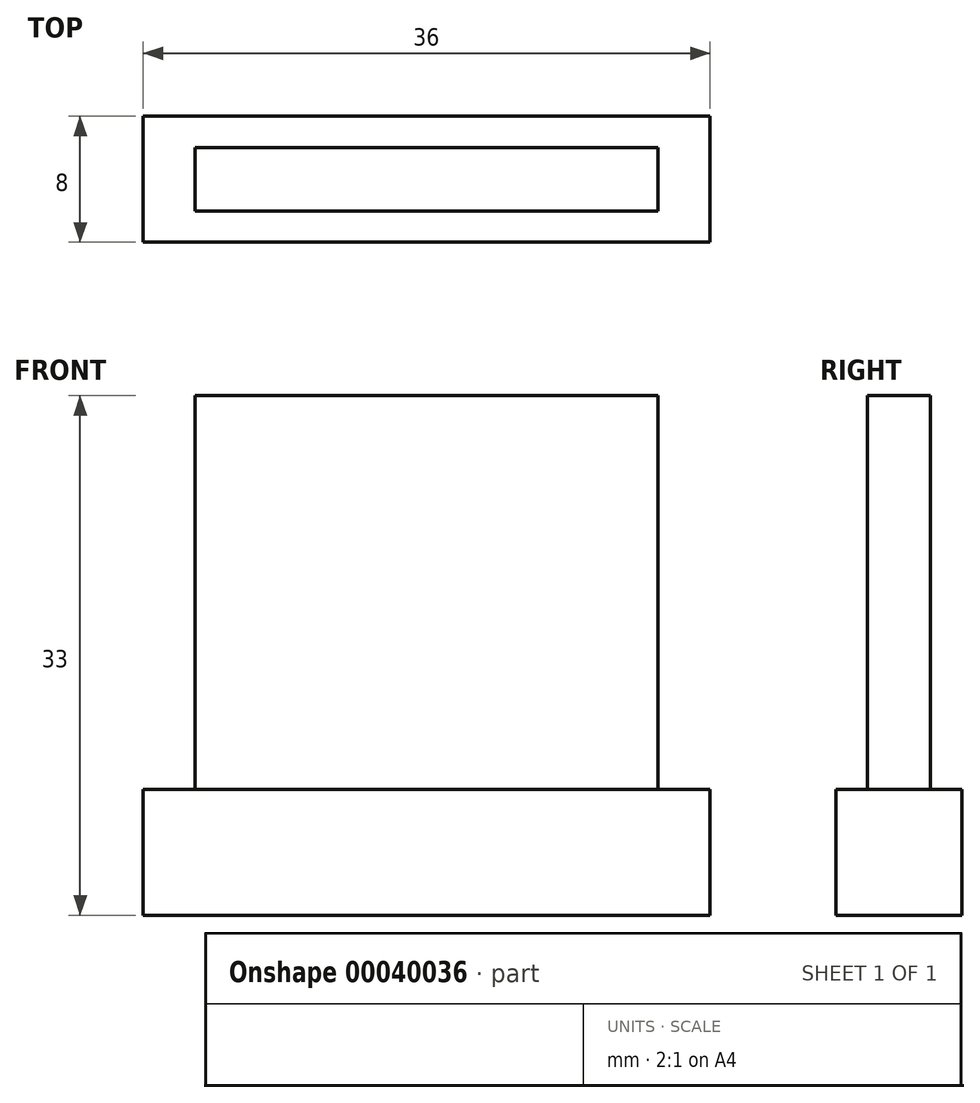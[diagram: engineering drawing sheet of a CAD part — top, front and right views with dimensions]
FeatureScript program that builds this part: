
annotation { "Feature Type Name" : "Feature", "Feature Type Description" : "" }
export const myFeature = defineFeature(function(context is Context, id is Id, definition is map)
    precondition{}
    {
        {
            var Q0;
            Q0=qCreatedBy(makeId("Top.planeOp"),FACE);
            var sketch = newSketch(context, id + "F0", { "sketchPlane" : qUnion([Q0])});
            skLineSegment(sketch, "E0.rect.bottom", {"start": v(18, -4) * mm, "end": v(-18, -4) * mm});
            skLineSegment(sketch, "E0.rect.top", {"start": v(18, 4) * mm, "end": v(-18, 4) * mm});
            skLineSegment(sketch, "E0.rect.left", {"start": v(18, -4) * mm, "end": v(18, 4) * mm});
            skLineSegment(sketch, "E0.rect.right", {"start": v(-18, -4) * mm, "end": v(-18, 4) * mm});
            skPoint(sketch, "E0.rect.middle", {"position": v(0, 0) * mm});
            skSolve(sketch);
        }
        {
            var Q0;
            Q0 = qSketchRegion(id + "F0", true);
            extrude(context, id + "F1", {"entities" : qUnion([Q0]), "depth" : 8 * mm});
        }
        {
            var Q0;
            Q0=makeQuery(id+"F1.opExtrude","CAP_FACE",FACE,{"disambiguationData":[OSD([sQuery(id+"F0.wireOp",EDGE,"E0.rect.bottom"),sQuery(id+"F0.wireOp",EDGE,"E0.rect.top"),sQuery(id+"F0.wireOp",EDGE,"E0.rect.left"),sQuery(id+"F0.wireOp",EDGE,"E0.rect.right")])],"isStart":false});
            var sketch = newSketch(context, id + "F2", { "sketchPlane" : qUnion([Q0])});
            skLineSegment(sketch, "E1.rect.bottom", {"start": v(14.7, -2) * mm, "end": v(-14.7, -2) * mm});
            skLineSegment(sketch, "E1.rect.top", {"start": v(14.7, 2) * mm, "end": v(-14.7, 2) * mm});
            skLineSegment(sketch, "E1.rect.left", {"start": v(14.7, -2) * mm, "end": v(14.7, 2) * mm});
            skLineSegment(sketch, "E1.rect.right", {"start": v(-14.7, -2) * mm, "end": v(-14.7, 2) * mm});
            skPoint(sketch, "E1.rect.middle", {"position": v(0, 0) * mm});
            skSolve(sketch);
        }
        {
            var Q0;
            Q0=makeQuery(id+"F2.imprint","IMPRINT",FACE,{"disambiguationData":[TD([[makeQuery(id+"F2.imprint","IMPRINT",EDGE,{"derivedFrom":sQuery(id+"F2.wireOp",EDGE,"E1.rect.bottom")}),-1.0]])]});
            extrude(context, id + "F3", {"entities" : qUnion([Q0]), "operationType" : NewBodyOperationType.ADD, "depth" : 25 * mm});
        }
    });
